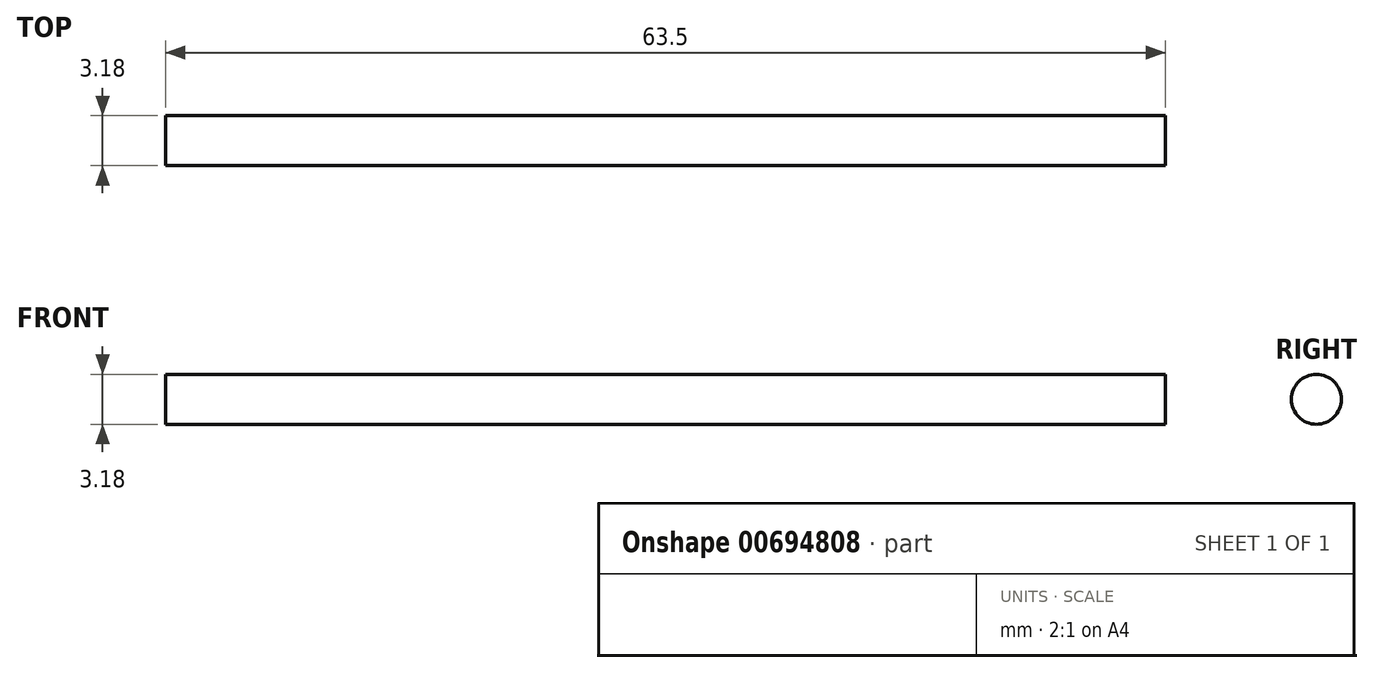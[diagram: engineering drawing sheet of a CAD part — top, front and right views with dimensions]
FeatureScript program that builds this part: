
annotation { "Feature Type Name" : "Feature", "Feature Type Description" : "" }
export const myFeature = defineFeature(function(context is Context, id is Id, definition is map)
    precondition{}
    {
        {
            var Q0;
            Q0=qCreatedBy(makeId("Right.planeOp"),FACE);
            var sketch = newSketch(context, id + "F0", { "sketchPlane" : qUnion([Q0])});
            skCircle(sketch, "E0", {"center": v(0, 0) * mm, "radius": 1.59 * mm});
            skSolve(sketch);
        }
        {
            var Q0;
            Q0 = qSketchRegion(id + "F0", true);
            extrude(context, id + "F1", {"entities" : qUnion([Q0]), "depth" : 63.5 * mm, "offsetDistance" : 25.4 * mm});
        }
    });
